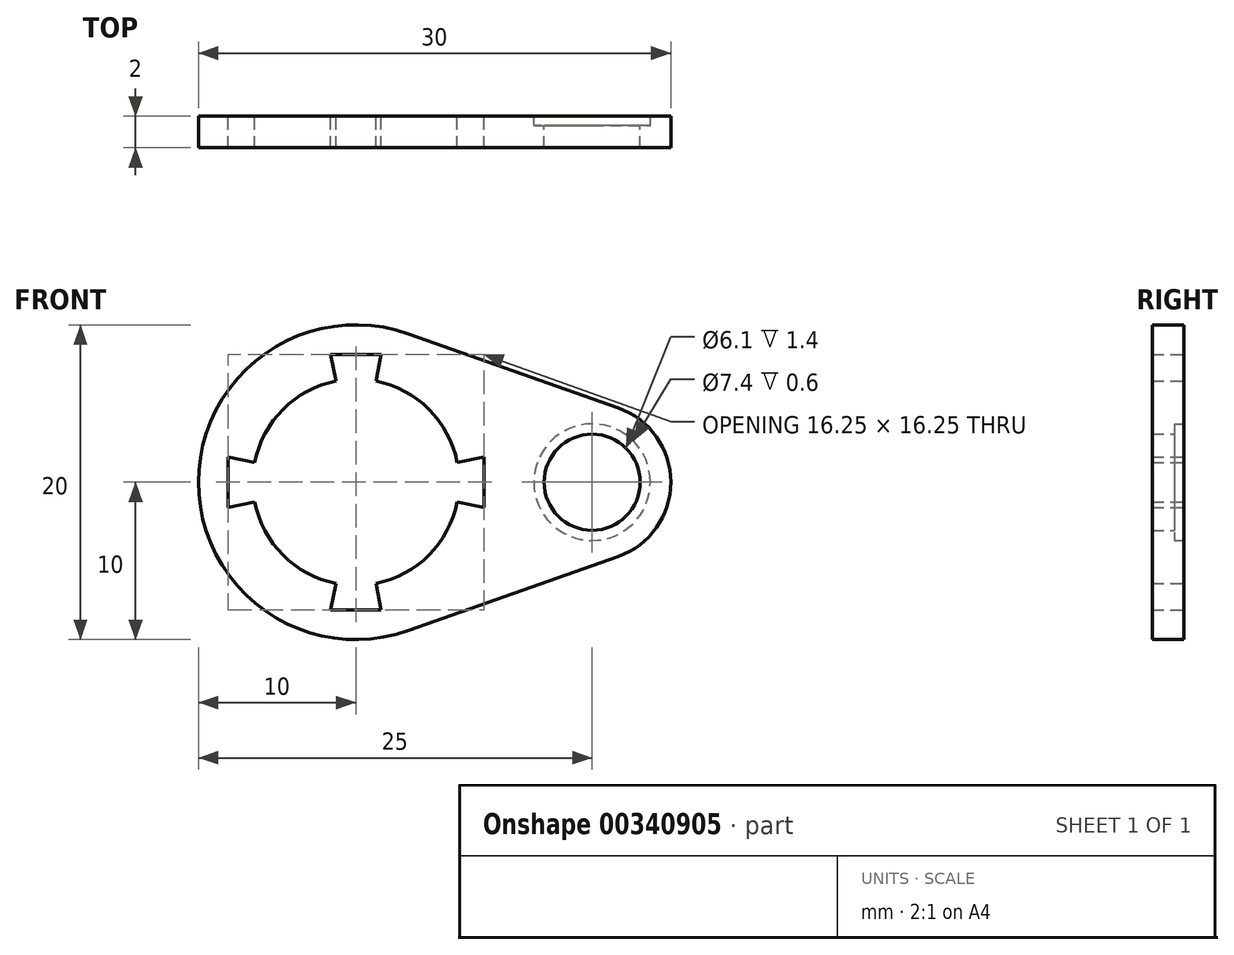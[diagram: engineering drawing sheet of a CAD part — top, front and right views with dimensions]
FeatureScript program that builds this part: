
annotation { "Feature Type Name" : "Feature", "Feature Type Description" : "" }
export const myFeature = defineFeature(function(context is Context, id is Id, definition is map)
    precondition{}
    {
        {
            var Q0;
            Q0=qCreatedBy(makeId("Front.planeOp"),FACE);
            var sketch = newSketch(context, id + "F0", { "sketchPlane" : qUnion([Q0])});
            skCircle(sketch, "E0", {"center": v(0, 0) * mm, "radius": 6.55 * mm});
            skLineSegment(sketch, "E1", {"start": v(-1.27, 6.43) * mm, "end": v(-1.6, 8.13) * mm});
            skLineSegment(sketch, "E2", {"start": v(-1.6, 8.13) * mm, "end": v(1.6, 8.13) * mm});
            skLineSegment(sketch, "E3", {"start": v(1.6, 8.13) * mm, "end": v(1.27, 6.43) * mm});
            skLineSegment(sketch, "E4.1.0", {"start": v(-8.13, -1.6) * mm, "end": v(-8.13, 1.6) * mm});
            skLineSegment(sketch, "E4.1.1", {"start": v(-6.43, -1.27) * mm, "end": v(-8.13, -1.6) * mm});
            skLineSegment(sketch, "E4.1.2", {"start": v(-8.13, 1.6) * mm, "end": v(-6.43, 1.27) * mm});
            skLineSegment(sketch, "E4.2.0", {"start": v(1.6, -8.13) * mm, "end": v(-1.6, -8.13) * mm});
            skLineSegment(sketch, "E4.2.1", {"start": v(1.27, -6.43) * mm, "end": v(1.6, -8.13) * mm});
            skLineSegment(sketch, "E4.2.2", {"start": v(-1.6, -8.13) * mm, "end": v(-1.27, -6.43) * mm});
            skLineSegment(sketch, "E4.3.0", {"start": v(8.13, 1.6) * mm, "end": v(8.13, -1.6) * mm});
            skLineSegment(sketch, "E4.3.1", {"start": v(6.43, 1.27) * mm, "end": v(8.13, 1.6) * mm});
            skLineSegment(sketch, "E4.3.2", {"start": v(8.13, -1.6) * mm, "end": v(6.43, -1.27) * mm});
            skArc(sketch, "E5", {"start": v(3.33, 9.43) * mm, "mid": v(-10, 0) * mm, "end": v(3.33, -9.43) * mm});
            skLineSegment(sketch, "E6", {"start": v(3.33, 9.43) * mm, "end": v(16.67, 4.71) * mm});
            skLineSegment(sketch, "E7", {"start": v(3.33, -9.43) * mm, "end": v(16.67, -4.71) * mm});
            skArc(sketch, "E8", {"start": v(16.67, -4.71) * mm, "mid": v(20, 0) * mm, "end": v(16.67, 4.71) * mm});
            skSolve(sketch);
        }
        {
            var Q0;
            {var subQ2=sQuery(id+"F0.wireOp",EDGE,"E1");Q0=makeQuery(id+"F0.imprint","IMPRINT",FACE,{"disambiguationData":[TD([[makeQuery(id+"F0.imprint","IMPRINT",EDGE,{"derivedFrom":subQ2}),1.0]])]});}
            extrude(context, id + "F1", {"entities" : qUnion([Q0]), "depth" : 2 * mm, "offsetDistance" : 25 * mm});
        }
        {
            var Q0;
            Q0=sQuery(id+"F0.wireOp",VERTEX,"E8.center");
            var Q1;
            Q1=makeQuery(id+"F1.opExtrude","SWEPT_BODY",BODY,{"disambiguationData":[OSD([sQuery(id+"F0.wireOp",EDGE,"E0"),sQuery(id+"F0.wireOp",EDGE,"E1"),sQuery(id+"F0.wireOp",EDGE,"E2"),sQuery(id+"F0.wireOp",EDGE,"E3"),sQuery(id+"F0.wireOp",EDGE,"E4.1.0"),sQuery(id+"F0.wireOp",EDGE,"E4.1.1"),sQuery(id+"F0.wireOp",EDGE,"E4.1.2"),sQuery(id+"F0.wireOp",EDGE,"E4.2.0"),sQuery(id+"F0.wireOp",EDGE,"E4.2.1"),sQuery(id+"F0.wireOp",EDGE,"E4.2.2"),sQuery(id+"F0.wireOp",EDGE,"E4.3.0"),sQuery(id+"F0.wireOp",EDGE,"E4.3.1"),sQuery(id+"F0.wireOp",EDGE,"E4.3.2"),sQuery(id+"F0.wireOp",EDGE,"E5"),sQuery(id+"F0.wireOp",EDGE,"E6"),sQuery(id+"F0.wireOp",EDGE,"E7"),sQuery(id+"F0.wireOp",EDGE,"E8")])]});
            hole(context, id + "F2", {"style" : HoleStyle.C_BORE, "endStyle" : HoleEndStyle.THROUGH, "oppositeDirection" : true, "holeDiameter" : 6.1 * mm, "cBoreDiameter" : 7.4 * mm, "cBoreDepth" : 0.6 * mm, "majorDiameter" : 5 * mm, "isTappedThrough" : true, "tappedDepth" : 12 * mm, "tapClearance" : 3, "locations" : qUnion([Q0]), "scope" : qUnion([Q1])});
        }
    });
